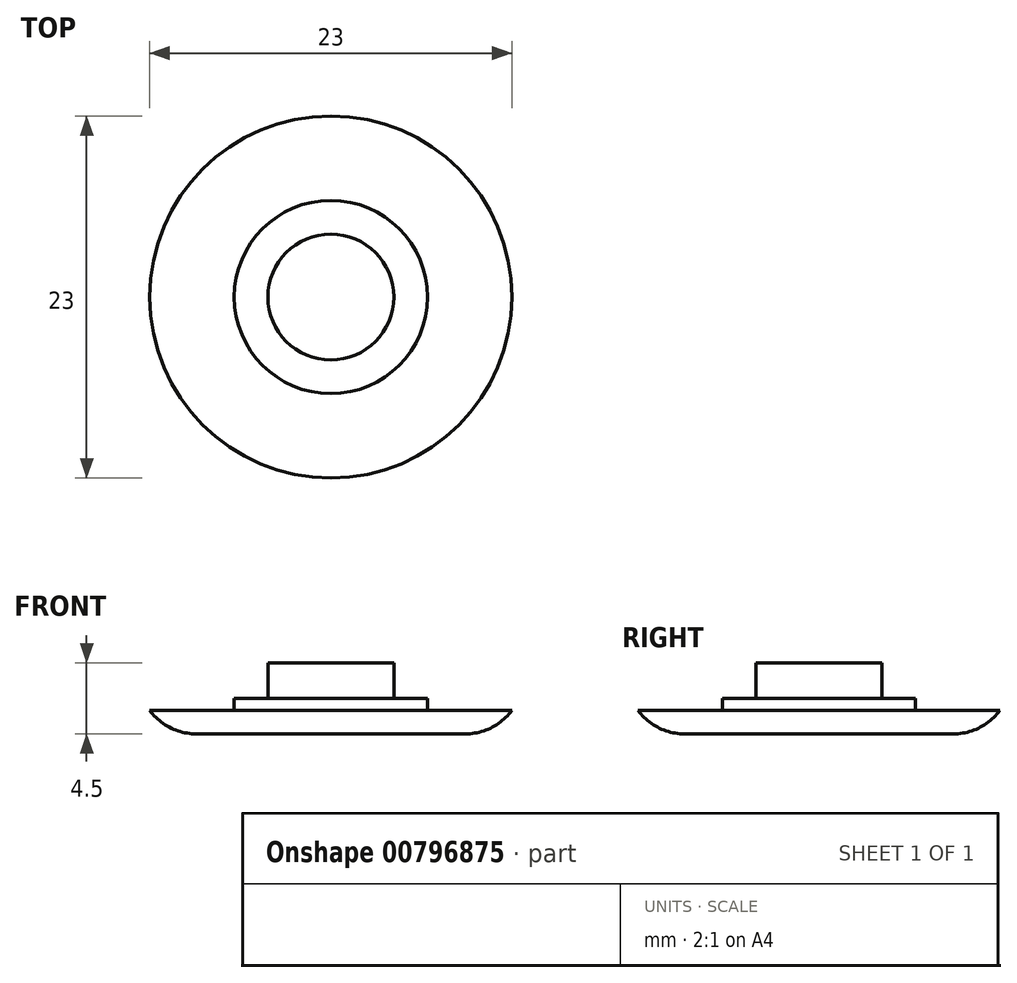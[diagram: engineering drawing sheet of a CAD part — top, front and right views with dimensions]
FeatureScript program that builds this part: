
annotation { "Feature Type Name" : "Feature", "Feature Type Description" : "" }
export const myFeature = defineFeature(function(context is Context, id is Id, definition is map)
    precondition{}
    {
        {
            var Q0;
            Q0=qCreatedBy(makeId("Top.planeOp"),FACE);
            var sketch = newSketch(context, id + "F0", { "sketchPlane" : qUnion([Q0])});
            skCircle(sketch, "E0", {"center": v(0, 0) * mm, "radius": 11.5 * mm});
            skSolve(sketch);
        }
        {
            var Q0;
            Q0=makeQuery(id+"F0.imprint","IMPRINT",FACE,{"disambiguationData":[TD([[makeQuery(id+"F0.imprint","IMPRINT",EDGE,{"derivedFrom":sQuery(id+"F0.wireOp",EDGE,"E0")}),1.0]])]});
            extrude(context, id + "F1", {"entities" : qUnion([Q0]), "depth" : 1.5 * mm, "offsetDistance" : 25.4 * mm});
        }
        {
            var Q0;
            Q0=makeQuery(id+"F1.opExtrude","CAP_FACE",FACE,{"disambiguationData":[OSD([sQuery(id+"F0.wireOp",EDGE,"E0")])],"isStart":false});
            var sketch = newSketch(context, id + "F2", { "sketchPlane" : qUnion([Q0])});
            skCircle(sketch, "E1", {"center": v(0, 0) * mm, "radius": 4 * mm});
            skSolve(sketch);
        }
        {
            var Q0;
            Q0=makeQuery(id+"F2.imprint","IMPRINT",FACE,{"disambiguationData":[TD([[makeQuery(id+"F2.imprint","IMPRINT",EDGE,{"derivedFrom":sQuery(id+"F2.wireOp",EDGE,"E1")}),-1.0]])]});
            var sketch = newSketch(context, id + "F3", { "sketchPlane" : qUnion([Q0])});
            skCircle(sketch, "E2", {"center": v(0, 0) * mm, "radius": 6.14 * mm});
            skSolve(sketch);
        }
        {
            var Q0;
            Q0=makeQuery(id+"F3.imprint","IMPRINT",FACE,{"disambiguationData":[TD([[makeQuery(id+"F3.imprint","IMPRINT",EDGE,{"derivedFrom":sQuery(id+"F3.wireOp",EDGE,"E2")}),1.0]])]});
            extrude(context, id + "F4", {"entities" : qUnion([Q0]), "operationType" : NewBodyOperationType.ADD, "depth" : 0.76 * mm, "offsetDistance" : 25.4 * mm});
        }
        {
            var Q0;
            Q0=makeQuery(id+"F2.imprint","IMPRINT",FACE,{"disambiguationData":[TD([[makeQuery(id+"F2.imprint","IMPRINT",EDGE,{"derivedFrom":sQuery(id+"F2.wireOp",EDGE,"E1")}),1.0]])]});
            extrude(context, id + "F5", {"entities" : qUnion([Q0]), "operationType" : NewBodyOperationType.ADD, "depth" : 3 * mm, "offsetDistance" : 25.4 * mm});
        }
        {
            var Q0;
            Q0=makeQuery(id+"F1.opExtrude","CAP_EDGE",EDGE,{"disambiguationData":[OSD([sQuery(id+"F0.wireOp",EDGE,"E0")])],"isStart":true});
            fillet(context, id + "F6", {"entities" : qUnion([Q0]), "radius" : 3.68 * mm, "tangentPropagation" : true, "allowEdgeOverflow" : false});
        }
    });
